# Revit family: Speciality_Equipment-Cord_Reel-Hubbell_Wiring-System_K5-HBLC25163C
name_source: partatom
category: Specialty Equipment
revit_build: Autodesk Revit Architecture 2015 (Build: 20140606_1530(x64)
units: mm (PartAtom-declared; Revit-internal decimal feet)

## types (1)
- HBLC25163C
    Amps = 10 A
    Assembly Code = D5090900
    BIMobject category = Outlets & Sockets
    BIMobject category code = electrical-outlets-sockets
    BIMobject main category = Electrical
    BIMobject main category code = electrical
    Brand url = http://www.hubbell-wiring.com
    Cover Material = Metal-Hubbell-Black
    Default Elevation = 0 "
    Description = Reel with a Hubbell HBL5969VBLK connector, yellow.
    Design country = United States
    Edition number = 1
    Electrical Connector Description = Commercial Cord Reel
    Hardware Material = Metal-Hubbell-Yellow
    IFC Classification = Electric Distribution
    Manufacturer = Hubbell Wiring Device-Kellems
    Manufacturer country = United States
    Manufacturer name = Hubbell Wiring Device-Kellems
    Masterformat 2014 Code = 26 05 33.16
    Masterformat 2014 Description = Boxes for Electrical Systems
    Material main = Steel
    Model = HBLC25163C
    NBS Reference Code = 62-38
    NBS Reference Description = Hoses And Hose Reels
    Nominal height = 0 "
    Nominal width = 0 "
    OmniClass Code = 23-35 33 17 11
    OmniClass Description = Electrical Cable Reels
    Product Documentation Link = https://hubbellcdn.com
    Product Guid = b04c4e90-8c66-4635-b28a-cdfa7a0f4381
    Product Page URL = https://www.hubbell.com
    Product SKU = Cord-and-Cable-Reels-HBLC25163C
    Product data url = https://bimobject.com
    Product family = Wire/Cable/Hose Management
    Product group = Cord Reels
    Product url = https://www.hubbell.com
    QR code = http://bimobject.com
    Technical description = https://hubbellcdn.com
    UNSPSC Code = 26121635
    URL = http://www.hubbell-wiring.com
    Uniclass 1.4 Code = L882
    Uniclass 1.4 Description = Hoses, hose reels and enclosures/cabinets
    Uniclass 2.0 Code = PR-62-38
    Uniclass 2.0 Description = Hoses And Hose Reels
    Uniclass 2015 Code = Pr_65_52_38
    Uniclass 2015 Name = Hoses, hose reels and ancillaries
    Voltage = 125 V
    Wattage = 1250 W
    Weight Net (Kg) = 0

## geometry (parser evidence)
native form markers: Blend x2, Sweep x3
no freeform markers — native parametric forms only
